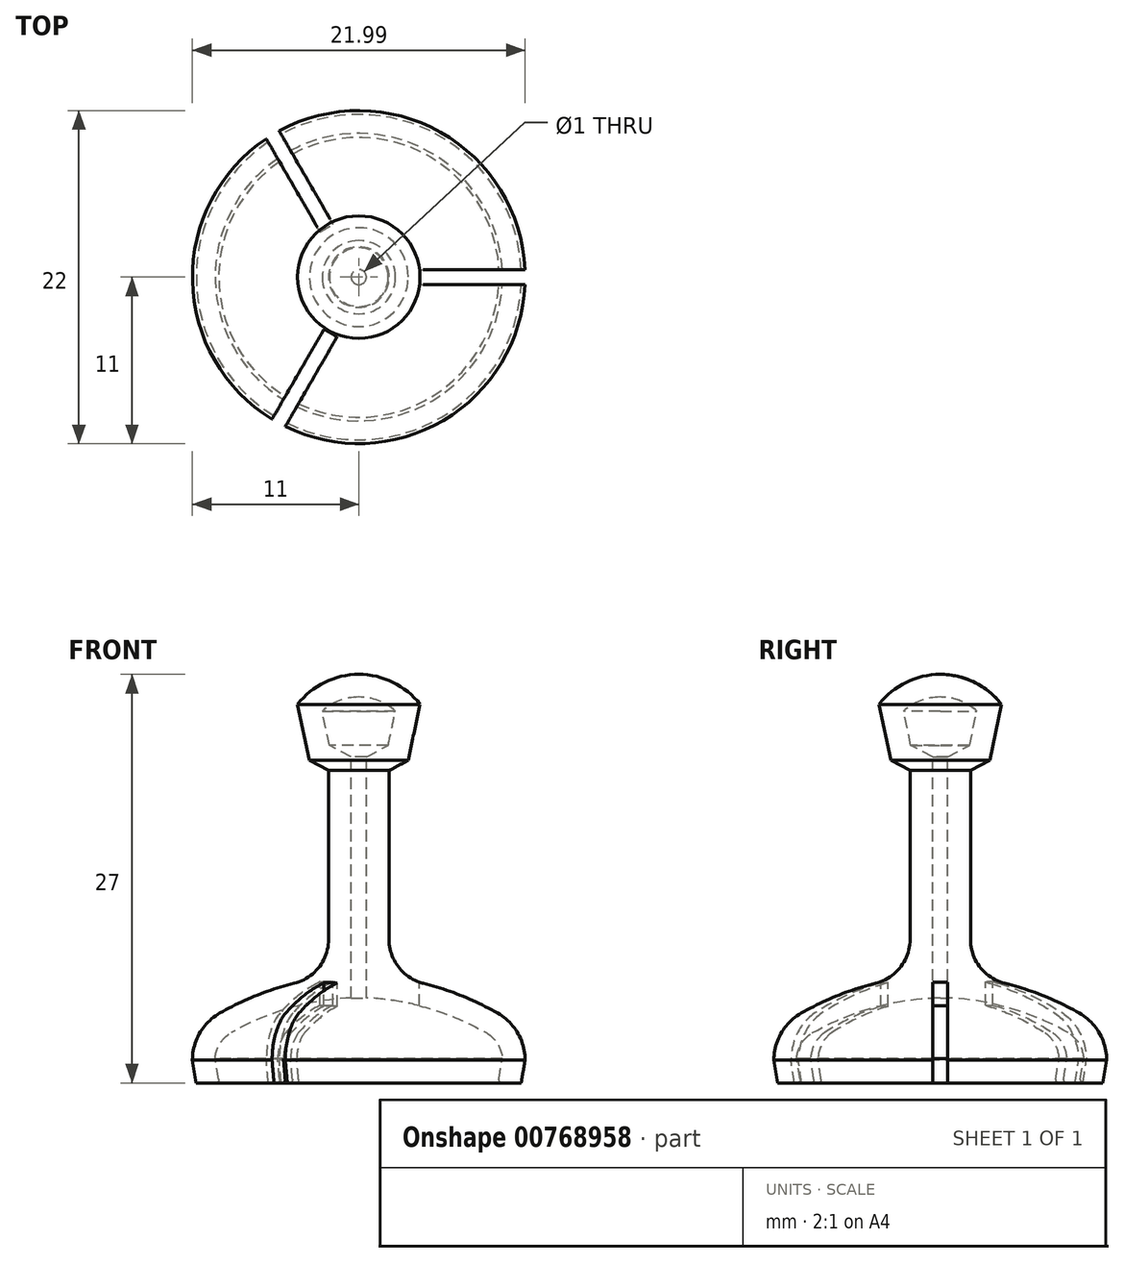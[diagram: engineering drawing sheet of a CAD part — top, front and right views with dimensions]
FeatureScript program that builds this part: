
annotation { "Feature Type Name" : "Feature", "Feature Type Description" : "" }
export const myFeature = defineFeature(function(context is Context, id is Id, definition is map)
    precondition{}
    {
        {
            var Q0;
            Q0=qCreatedBy(makeId("Right.planeOp"),FACE);
            var sketch = newSketch(context, id + "F0", { "sketchPlane" : qUnion([Q0])});
            skLineSegment(sketch, "E0", {"start": v(11, 0) * mm, "end": v(10.74, -1.5) * mm});
            skLineSegment(sketch, "E1", {"start": v(2, 5.5) * mm, "end": v(2, 19.14) * mm});
            skLineSegment(sketch, "E2", {"start": v(2, 19.14) * mm, "end": v(3.27, 19.82) * mm});
            skLineSegment(sketch, "E3", {"start": v(3.27, 19.82) * mm, "end": v(4.05, 23.52) * mm});
            skArc(sketch, "E4", {"start": v(4.05, 23.52) * mm, "mid": v(2.25, 24.98) * mm, "end": v(0, 25.5) * mm});
            skArc(sketch, "E5", {"start": v(9.2, 3.11) * mm, "mid": v(5.72, 4.67) * mm, "end": v(2, 5.5) * mm});
            skArc(sketch, "E6", {"start": v(9.2, 3.11) * mm, "mid": v(10.52, 1.8) * mm, "end": v(11, 0) * mm});
            skLineSegment(sketch, "E7", {"start": v(0, 25.5) * mm, "end": v(0, -1.5) * mm});
            skLineSegment(sketch, "E8", {"start": v(0, -1.5) * mm, "end": v(10.74, -1.5) * mm});
            skSolve(sketch);
        }
        {
            var Q0;
            Q0=makeQuery(id+"F0.imprint","IMPRINT",FACE,{"disambiguationData":[TD([[makeQuery(id+"F0.imprint","IMPRINT",EDGE,{"derivedFrom":sQuery(id+"F0.wireOp",EDGE,"E0")}),-1.0]])]});
            var Q1;
            Q1=sQuery(id+"F0.wireOp",EDGE,"E7");
            revolve(context, id + "F1", {"surfaceOperationType" : NewSurfaceOperationType.NEW, "entities" : qUnion([Q0]), "axis" : qUnion([Q1]), "revolveType" : RevolveType.FULL});
        }
        {
            var Q0;
            Q0=makeQuery(id+"F1.opRevolve","SWEPT_FACE",FACE,{"disambiguationData":[OSD([sQuery(id+"F0.wireOp",EDGE,"E8")])]});
            shell(context, id + "F2", {"entities" : qUnion([Q0]), "thickness" : 1.5 * mm});
        }
        {
            var Q0;
            Q0=makeQuery(id+"F1.opRevolve","SWEPT_EDGE",EDGE,{"disambiguationData":[OSD([sQuery(id+"F0.wireOp",EDGE,"E1"),sQuery(id+"F0.wireOp",EDGE,"E5")])]});
            fillet(context, id + "F3", {"entities" : qUnion([Q0]), "radius" : 3 * mm, "tangentPropagation" : true, "allowEdgeOverflow" : false});
        }
        {
            var Q0;
            Q0=makeQuery(id+"F2.opShell","OFFSET_EDGE",EDGE,{"disambiguationData":[OSD([sQuery(id+"F0.wireOp",EDGE,"E0"),sQuery(id+"F0.wireOp",EDGE,"E8")])]});
            fillet(context, id + "F4", {"entities" : qUnion([Q0]), "radius" : 0.2 * mm, "tangentPropagation" : true, "allowEdgeOverflow" : false});
        }
        {
            var Q0;
            Q0=qCreatedBy(makeId("Top.planeOp"),FACE);
            var sketch = newSketch(context, id + "F5", { "sketchPlane" : qUnion([Q0])});
            skLineSegment(sketch, "E9.bottom", {"start": v(12, -0.5) * mm, "end": v(4, -0.5) * mm});
            skLineSegment(sketch, "E9.top", {"start": v(12, 0.5) * mm, "end": v(4, 0.5) * mm});
            skLineSegment(sketch, "E9.left", {"start": v(12, -0.5) * mm, "end": v(12, 0.5) * mm});
            skLineSegment(sketch, "E9.right", {"start": v(4, -0.5) * mm, "end": v(4, 0.5) * mm});
            skPoint(sketch, "E9.middle", {"position": v(8, 0) * mm});
            skLineSegment(sketch, "E10.1.0", {"start": v(-6.3, -10.37) * mm, "end": v(-5.44, -10.87) * mm});
            skLineSegment(sketch, "E10.1.1", {"start": v(-2.3, -3.44) * mm, "end": v(-1.44, -3.94) * mm});
            skPoint(sketch, "E10.1.2", {"position": v(-3.87, -7.16) * mm});
            skLineSegment(sketch, "E10.1.3", {"start": v(-5.44, -10.87) * mm, "end": v(-1.44, -3.94) * mm});
            skLineSegment(sketch, "E10.1.4", {"start": v(-6.3, -10.37) * mm, "end": v(-2.3, -3.44) * mm});
            skLineSegment(sketch, "E10.2.0", {"start": v(-5.7, 10.42) * mm, "end": v(-6.56, 9.92) * mm});
            skLineSegment(sketch, "E10.2.1", {"start": v(-1.7, 3.49) * mm, "end": v(-2.56, 2.99) * mm});
            skPoint(sketch, "E10.2.2", {"position": v(-4.13, 6.7) * mm});
            skLineSegment(sketch, "E10.2.3", {"start": v(-6.56, 9.92) * mm, "end": v(-2.56, 2.99) * mm});
            skLineSegment(sketch, "E10.2.4", {"start": v(-5.7, 10.42) * mm, "end": v(-1.7, 3.49) * mm});
            skPoint(sketch, "E10.center", {"position": v(0, -0.15) * mm});
            skLineSegment(sketch, "E10.anchor1", {"start": v(0, -0.15) * mm, "end": v(8, 0) * mm, "construction": true});
            skLineSegment(sketch, "E10.anchor2", {"start": v(0, -0.15) * mm, "end": v(-4.13, 6.7) * mm, "construction": true});
            skSolve(sketch);
        }
        {
            var Q0;
            Q0=makeQuery(id+"F5.imprint","IMPRINT",FACE,{"disambiguationData":[TD([[makeQuery(id+"F5.imprint","IMPRINT",EDGE,{"derivedFrom":sQuery(id+"F5.wireOp",EDGE,"E10.2.0")}),1.0]])]});
            var Q1;
            Q1=makeQuery(id+"F5.imprint","IMPRINT",FACE,{"disambiguationData":[TD([[makeQuery(id+"F5.imprint","IMPRINT",EDGE,{"derivedFrom":sQuery(id+"F5.wireOp",EDGE,"E10.1.0")}),1.0]])]});
            var Q2;
            Q2=makeQuery(id+"F5.imprint","IMPRINT",FACE,{"disambiguationData":[TD([[makeQuery(id+"F5.imprint","IMPRINT",EDGE,{"derivedFrom":sQuery(id+"F5.wireOp",EDGE,"E9.bottom")}),-1.0]])]});
            extrude(context, id + "F6", {"entities" : qUnion([Q0, Q1, Q2]), "operationType" : NewBodyOperationType.REMOVE, "oppositeDirection" : true, "depth" : 15 * mm, "offsetDistance" : 25 * mm, "hasSecondDirection" : true, "secondDirectionOppositeDirection" : false, "secondDirectionDepth" : 15 * mm});
        }
    });
